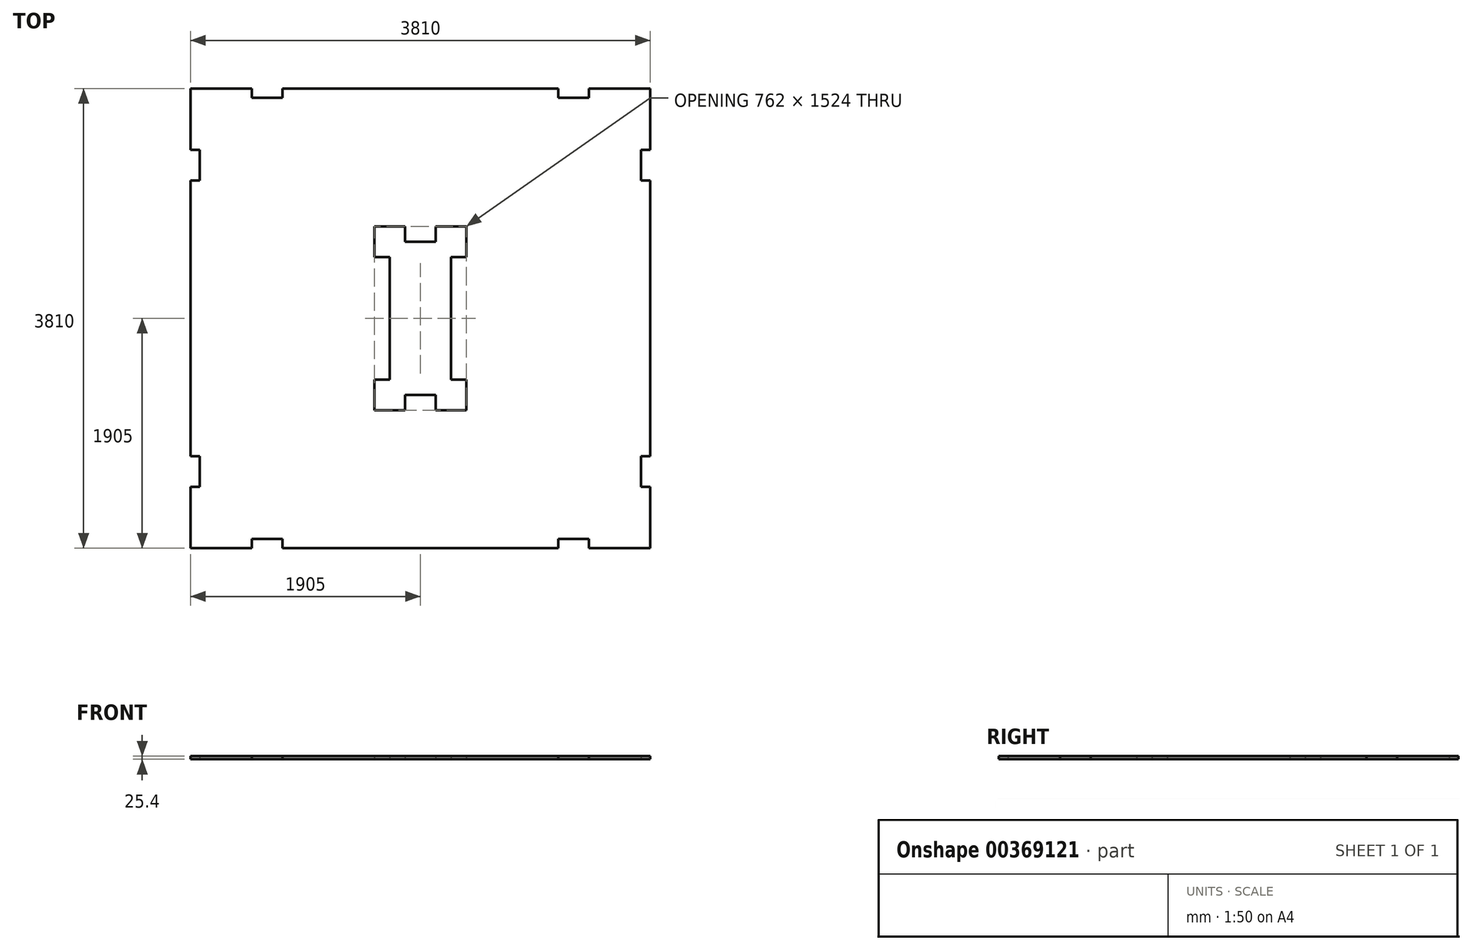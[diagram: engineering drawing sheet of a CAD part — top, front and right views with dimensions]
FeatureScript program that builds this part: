
annotation { "Feature Type Name" : "Feature", "Feature Type Description" : "" }
export const myFeature = defineFeature(function(context is Context, id is Id, definition is map)
    precondition{}
    {
        {
            var Q0;
            Q0=qCreatedBy(makeId("Top.planeOp"),FACE);
            var sketch = newSketch(context, id + "F0", { "sketchPlane" : qUnion([Q0])});
            skLineSegment(sketch, "E0.bottom", {"start": v(1905, 1905) * mm, "end": v(1397, 1905) * mm});
            skLineSegment(sketch, "E0.top", {"start": v(1143, -1905) * mm, "end": v(-1143, -1905) * mm});
            skLineSegment(sketch, "E0.left", {"start": v(1905, 1905) * mm, "end": v(1905, 1397) * mm});
            skLineSegment(sketch, "E0.right", {"start": v(-1905, 1905) * mm, "end": v(-1905, 1397) * mm});
            skPoint(sketch, "E0.middle", {"position": v(0, 0) * mm});
            skLineSegment(sketch, "E1", {"start": v(-1828.8, 1397) * mm, "end": v(-1828.8, 1397) * mm});
            skLineSegment(sketch, "E2.trimOffspring", {"start": v(-1905, 1143) * mm, "end": v(-1905, -1143) * mm});
            skLineSegment(sketch, "E3", {"start": v(-1905, 1905) * mm, "end": v(-1397, 1905) * mm});
            skLineSegment(sketch, "E4", {"start": v(-1397, 1905) * mm, "end": v(-1397, 1828.8) * mm});
            skLineSegment(sketch, "E5", {"start": v(-1397, 1828.8) * mm, "end": v(-1143, 1828.8) * mm});
            skLineSegment(sketch, "E6", {"start": v(-1143, 1905) * mm, "end": v(-1143, 1828.8) * mm});
            skLineSegment(sketch, "E7", {"start": v(-1905, -1905) * mm, "end": v(-1905, -1397) * mm});
            skLineSegment(sketch, "E8", {"start": v(-1905, -1397) * mm, "end": v(-1828.8, -1397) * mm});
            skLineSegment(sketch, "E9", {"start": v(-1905, -1143) * mm, "end": v(-1828.8, -1143) * mm});
            skLineSegment(sketch, "E10", {"start": v(-1828.8, -1143) * mm, "end": v(-1828.8, -1397) * mm});
            skLineSegment(sketch, "E11", {"start": v(-1905, -1905) * mm, "end": v(-1397, -1905) * mm});
            skLineSegment(sketch, "E12", {"start": v(-1397, -1905) * mm, "end": v(-1397, -1828.8) * mm});
            skLineSegment(sketch, "E13", {"start": v(-1397, -1828.8) * mm, "end": v(-1143, -1828.8) * mm});
            skLineSegment(sketch, "E14", {"start": v(-1143, -1828.8) * mm, "end": v(-1143, -1905) * mm});
            skLineSegment(sketch, "E15.trimOffspring", {"start": v(-1397, -1905) * mm, "end": v(-1905, -1905) * mm});
            skLineSegment(sketch, "E16", {"start": v(1905, -1905) * mm, "end": v(1397, -1905) * mm});
            skLineSegment(sketch, "E17", {"start": v(1397, -1905) * mm, "end": v(1397, -1828.8) * mm});
            skLineSegment(sketch, "E18", {"start": v(1397, -1828.8) * mm, "end": v(1143, -1828.8) * mm});
            skLineSegment(sketch, "E19", {"start": v(1143, -1828.8) * mm, "end": v(1143, -1905) * mm});
            skLineSegment(sketch, "E20", {"start": v(1905, -1905) * mm, "end": v(1905, -1397) * mm});
            skLineSegment(sketch, "E21", {"start": v(1905, -1397) * mm, "end": v(1828.8, -1397) * mm});
            skLineSegment(sketch, "E22", {"start": v(1828.8, -1397) * mm, "end": v(1828.8, -1143) * mm});
            skLineSegment(sketch, "E23", {"start": v(1828.8, -1143) * mm, "end": v(1905, -1143) * mm});
            skLineSegment(sketch, "E24.trimOffspring", {"start": v(1905, -1397) * mm, "end": v(1905, -1905) * mm});
            skLineSegment(sketch, "E25", {"start": v(1905, 1397) * mm, "end": v(1828.8, 1397) * mm});
            skLineSegment(sketch, "E26", {"start": v(1828.8, 1397) * mm, "end": v(1828.8, 1143) * mm});
            skLineSegment(sketch, "E27", {"start": v(1905, 1143) * mm, "end": v(1828.8, 1143) * mm});
            skLineSegment(sketch, "E28.trimOffspring", {"start": v(1905, 1143) * mm, "end": v(1905, -1143) * mm});
            skLineSegment(sketch, "E29", {"start": v(1397, 1905) * mm, "end": v(1397, 1828.8) * mm});
            skLineSegment(sketch, "E30", {"start": v(1143, 1905) * mm, "end": v(1143, 1828.8) * mm});
            skLineSegment(sketch, "E31", {"start": v(1397, 1828.8) * mm, "end": v(1143, 1828.8) * mm});
            skLineSegment(sketch, "E32.trimOffspring", {"start": v(1143, 1905) * mm, "end": v(-1143, 1905) * mm});
            skLineSegment(sketch, "E33.trimOffspring", {"start": v(-1905, -1397) * mm, "end": v(-1905, -1905) * mm});
            skPoint(sketch, "E34.top.start.orphan", {"position": v(-254, 635) * mm});
            skPoint(sketch, "E34.right.end.orphan", {"position": v(254, 635) * mm});
            skPoint(sketch, "E34.bottom.end.orphan", {"position": v(254, -635) * mm});
            skPoint(sketch, "E34.bottom.start.orphan", {"position": v(-254, -635) * mm});
            skLineSegment(sketch, "E35.trimOffspring", {"start": v(-1397, 1905) * mm, "end": v(-1905, 1905) * mm});
            skLineSegment(sketch, "E36.bottom", {"start": v(127, 127) * mm, "end": v(-127, 127) * mm});
            skLineSegment(sketch, "E36.top", {"start": v(127, -127) * mm, "end": v(-127, -127) * mm});
            skLineSegment(sketch, "E36.left", {"start": v(127, 127) * mm, "end": v(127, -127) * mm});
            skLineSegment(sketch, "E36.right", {"start": v(-127, 127) * mm, "end": v(-127, -127) * mm});
            skLineSegment(sketch, "E37", {"start": v(-1905, 1397) * mm, "end": v(-1828.8, 1397) * mm});
            skLineSegment(sketch, "E38", {"start": v(-1828.8, 1397) * mm, "end": v(-1828.8, 1143) * mm});
            skLineSegment(sketch, "E39", {"start": v(-1828.8, 1143) * mm, "end": v(-1905, 1143) * mm});
            skLineSegment(sketch, "E40.bottom", {"start": v(-127, 762) * mm, "end": v(-381, 762) * mm});
            skLineSegment(sketch, "E40.top", {"start": v(-127, 508) * mm, "end": v(-381, 508) * mm});
            skLineSegment(sketch, "E40.left", {"start": v(-127, 762) * mm, "end": v(-127, 508) * mm});
            skLineSegment(sketch, "E40.right", {"start": v(-381, 762) * mm, "end": v(-381, 508) * mm});
            skLineSegment(sketch, "E41.bottom", {"start": v(381, 762) * mm, "end": v(127, 762) * mm});
            skLineSegment(sketch, "E41.top", {"start": v(381, 508) * mm, "end": v(127, 508) * mm});
            skLineSegment(sketch, "E41.left", {"start": v(381, 762) * mm, "end": v(381, 508) * mm});
            skLineSegment(sketch, "E41.right", {"start": v(127, 762) * mm, "end": v(127, 508) * mm});
            skLineSegment(sketch, "E42.bottom", {"start": v(381, -508) * mm, "end": v(127, -508) * mm});
            skLineSegment(sketch, "E42.top", {"start": v(381, -762) * mm, "end": v(127, -762) * mm});
            skLineSegment(sketch, "E42.left", {"start": v(381, -508) * mm, "end": v(381, -762) * mm});
            skLineSegment(sketch, "E42.right", {"start": v(127, -508) * mm, "end": v(127, -762) * mm});
            skLineSegment(sketch, "E43.bottom", {"start": v(-127, -508) * mm, "end": v(-381, -508) * mm});
            skLineSegment(sketch, "E43.top", {"start": v(-127, -762) * mm, "end": v(-381, -762) * mm});
            skLineSegment(sketch, "E43.left", {"start": v(-127, -508) * mm, "end": v(-127, -762) * mm});
            skLineSegment(sketch, "E43.right", {"start": v(-381, -508) * mm, "end": v(-381, -762) * mm});
            skLineSegment(sketch, "E44", {"start": v(-254, 635) * mm, "end": v(-254, -635) * mm});
            skLineSegment(sketch, "E45", {"start": v(-254, -635) * mm, "end": v(254, -635) * mm});
            skLineSegment(sketch, "E46", {"start": v(254, -635) * mm, "end": v(254, 635) * mm});
            skLineSegment(sketch, "E47", {"start": v(254, 635) * mm, "end": v(-254, 635) * mm});
            skSolve(sketch);
        }
        {
            var Q0;
            Q0=makeQuery(id+"F0.imprint","IMPRINT",FACE,{"disambiguationData":[TD([[makeQuery(id+"F0.imprint","IMPRINT",EDGE,{"derivedFrom":sQuery(id+"F0.wireOp",EDGE,"E0.top")}),-1.0]])]});
            extrude(context, id + "F1", {"entities" : qUnion([Q0]), "depth" : 25.4 * mm});
        }
    });
